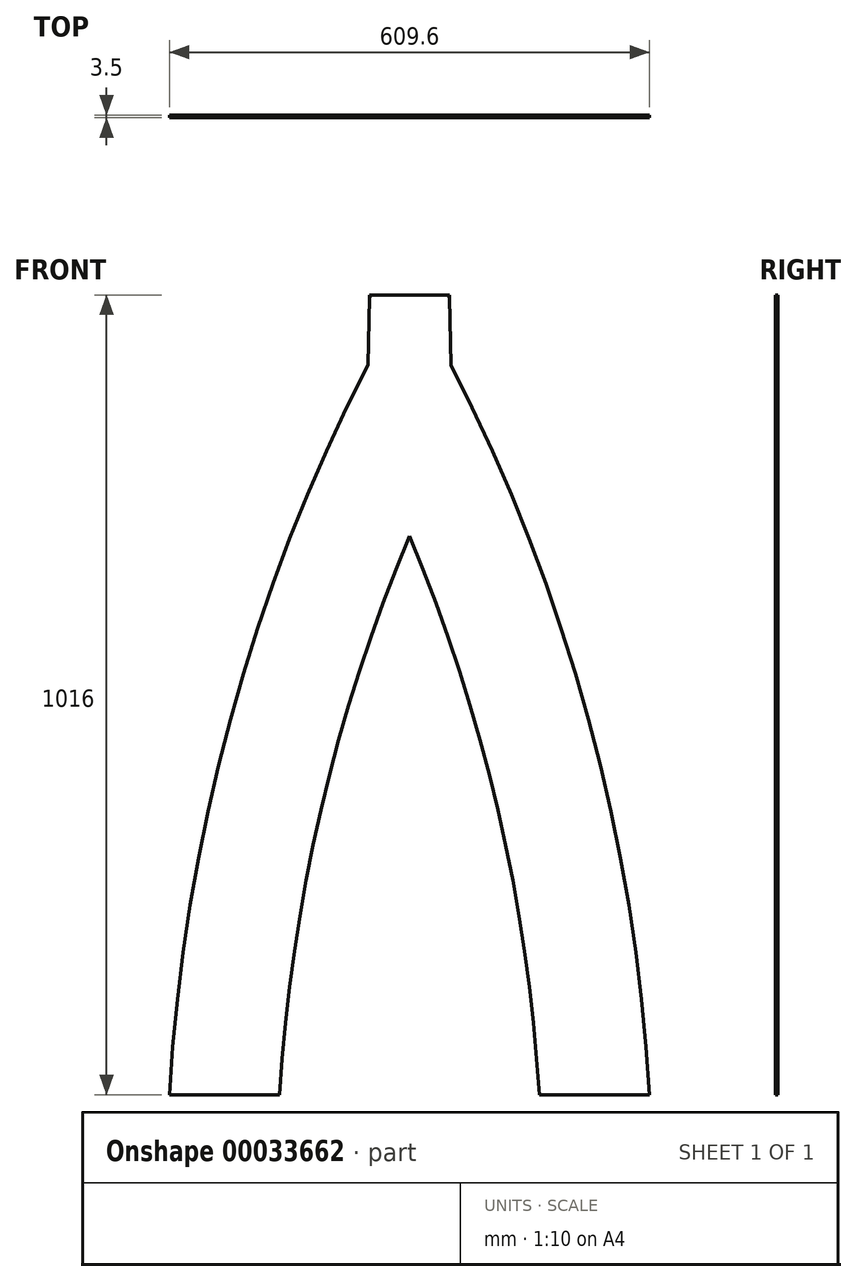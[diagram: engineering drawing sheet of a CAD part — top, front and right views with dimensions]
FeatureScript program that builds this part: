
annotation { "Feature Type Name" : "Feature", "Feature Type Description" : "" }
export const myFeature = defineFeature(function(context is Context, id is Id, definition is map)
    precondition{}
    {
        {
            assignVariable(context, id + "F0", {"name" : "Thickness", "anyValue" : 3.5});
        }
        {
            var Q0;
            Q0=qCreatedBy(makeId("Front.planeOp"),FACE);
            var sketch = newSketch(context, id + "F1", { "sketchPlane" : qUnion([Q0])});
            skLineSegment(sketch, "E0", {"start": v(34.8, 530.5) * mm, "end": v(34.8, -485.5) * mm, "construction": true});
            skLineSegment(sketch, "E1", {"start": v(34.8, 530.5) * mm, "end": v(-16, 530.5) * mm});
            skLineSegment(sketch, "E2", {"start": v(-130.06, -485.5) * mm, "end": v(-270, -485.5) * mm});
            skLineSegment(sketch, "E3.0", {"start": v(34.8, 441.6) * mm, "end": v(-17.87, 441.6) * mm, "construction": true});
            skPoint(sketch, "E4.orphan", {"position": v(34.8, -485.5) * mm});
            skArc(sketch, "E5", {"start": v(-17.87, 441.6) * mm, "mid": v(-192.67, -8.7) * mm, "end": v(-270, -485.5) * mm});
            skLineSegment(sketch, "E6", {"start": v(-16, 530.5) * mm, "end": v(-17.87, 441.6) * mm});
            skArc(sketch, "E7.0", {"start": v(34.8, 224.11) * mm, "mid": v(-77.62, -123.73) * mm, "end": v(-130.06, -485.5) * mm});
            skArc(sketch, "E8.MirrorCS", {"start": v(34.8, 224.11) * mm, "mid": v(147.23, -123.73) * mm, "end": v(199.67, -485.5) * mm});
            skArc(sketch, "E9.MirrorCS", {"start": v(87.49, 441.6) * mm, "mid": v(262.28, -8.7) * mm, "end": v(339.6, -485.5) * mm});
            skLineSegment(sketch, "E10.MirrorCS", {"start": v(85.6, 530.5) * mm, "end": v(87.49, 441.6) * mm});
            skLineSegment(sketch, "E11.MirrorCS", {"start": v(34.8, 530.5) * mm, "end": v(85.6, 530.5) * mm});
            skLineSegment(sketch, "E12.MirrorCS", {"start": v(199.67, -485.5) * mm, "end": v(339.6, -485.5) * mm});
            skSolve(sketch);
        }
        {
            var Q0;
            {var subQ5=sQuery(id+"F1.wireOp",EDGE,"E2");Q0=makeQuery(id+"F1.imprint","IMPRINT",FACE,{"disambiguationData":[TD([[makeQuery(id+"F1.imprint","IMPRINT",EDGE,{"derivedFrom":subQ5}),-1.0]])]});}
            var Q1;
            {var subQ5=sQuery(id+"F1.wireOp",EDGE,"E1");Q1=makeQuery(id+"F1.imprint","IMPRINT",FACE,{"disambiguationData":[TD([[makeQuery(id+"F1.imprint","IMPRINT",EDGE,{"derivedFrom":subQ5}),1.0]])]});}
            extrude(context, id + "F2", {"entities" : qUnion([Q0, Q1]), "depth" : (getVariable(context, 'Thickness')) * mm});
        }
        {
            var Q0;
            Q0=makeQuery(id+"F2.opExtrude","SWEPT_FACE",FACE,{"disambiguationData":[OSD([sQuery(id+"F1.wireOp",EDGE,"E1"),sQuery(id+"F1.wireOp",EDGE,"b7036a95-6d76-4b20-8edb-37fe3cfd70320.MirrorCS")])]});
            var sketch = newSketch(context, id + "F3", { "sketchPlane" : qUnion([Q0])});
            skLineSegment(sketch, "E13.bottom", {"start": v(-16, 0) * mm, "end": v(85.6, 0) * mm, "construction": true});
            skLineSegment(sketch, "E13.top", {"start": v(-16, -88.9) * mm, "end": v(85.6, -88.9) * mm, "construction": true});
            skLineSegment(sketch, "E14", {"start": v(34.8, -88.9) * mm, "end": v(34.8, 0) * mm, "construction": true});
            skLineSegment(sketch, "E15", {"start": v(34.8, -88.9) * mm, "end": v(6.23, -88.9) * mm});
            skLineSegment(sketch, "E16", {"start": v(-16, 0) * mm, "end": v(6.23, -88.9) * mm});
            skLineSegment(sketch, "E17", {"start": v(-16, 0) * mm, "end": v(34.8, 0) * mm});
            skLineSegment(sketch, "E18.MirrorCS", {"start": v(85.6, 0) * mm, "end": v(34.8, 0) * mm});
            skLineSegment(sketch, "E19.MirrorCS", {"start": v(34.8, -88.9) * mm, "end": v(63.38, -88.9) * mm});
            skLineSegment(sketch, "E20.MirrorCS", {"start": v(85.6, 0) * mm, "end": v(63.38, -88.9) * mm});
            skLineSegment(sketch, "E21", {"start": v(6.23, -88.9) * mm, "end": v(-42.78, -88.9) * mm});
            skLineSegment(sketch, "E22", {"start": v(-42.78, -88.9) * mm, "end": v(-42.78, 0) * mm});
            skLineSegment(sketch, "E23", {"start": v(-42.78, 0) * mm, "end": v(122.7, 0) * mm});
            skLineSegment(sketch, "E24", {"start": v(122.7, 0) * mm, "end": v(129.1, -88.9) * mm});
            skLineSegment(sketch, "E25", {"start": v(129.1, -88.9) * mm, "end": v(85.6, -88.9) * mm});
            skLineSegment(sketch, "E26", {"start": v(85.6, -88.9) * mm, "end": v(63.38, -88.9) * mm});
            skSolve(sketch);
        }
        {
            var Q0;
            {var subQ2=sQuery(id+"F3.wireOp",EDGE,"E16");Q0=makeQuery(id+"F3.imprint","IMPRINT",FACE,{"disambiguationData":[TD([[makeQuery(id+"F3.imprint","IMPRINT",EDGE,{"derivedFrom":subQ2}),-1.0]])]});}
            var Q1;
            Q1=makeQuery(id+"F3.imprint","IMPRINT",FACE,{"disambiguationData":[TD([[makeQuery(id+"F3.imprint","IMPRINT",EDGE,{"derivedFrom":sQuery(id+"F3.wireOp",EDGE,"E20.MirrorCS")}),1.0]])]});
            var Q2;
            {var subQ0=sQuery(id+"F3.wireOp",EDGE,"E24");Q2=makeQuery(id+"F3.imprint","IMPRINT",FACE,{"disambiguationData":[TD([[makeQuery(id+"F3.imprint","IMPRINT",EDGE,{"derivedFrom":subQ0}),-1.0]])]});}
            var Q3;
            {var subQ2=sQuery(id+"F3.wireOp",EDGE,"E22");Q3=makeQuery(id+"F3.imprint","IMPRINT",FACE,{"disambiguationData":[TD([[makeQuery(id+"F3.imprint","IMPRINT",EDGE,{"derivedFrom":subQ2}),-1.0]])]});}
            extrude(context, id + "F4", {"entities" : qUnion([Q0, Q1, Q2, Q3]), "operationType" : NewBodyOperationType.REMOVE, "oppositeDirection" : true, "depth" : (getVariable(context, 'Thickness')) * mm});
        }
    });
